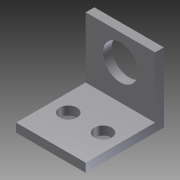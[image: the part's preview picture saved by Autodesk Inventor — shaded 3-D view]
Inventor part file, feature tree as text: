
AUTODESK INVENTOR PART (.ipt)
format: ipt  version: 2012 (Build 160160000, 160)  size: 105,472 bytes
history: native  units: in
note: dims shown in document units (in); Inventor stores cm internally (conversion verified against a paired STEP export)
features: extrude x3, sketch x3
ambient origin geometry x8: Origin, YZ Plane, XZ Plane, XY Plane, X Axis, Y Axis, Z Axis, Center Point
bodies: Solid1 (feature_tree)
feature tree (6):
  extrude  "Extrusion1"  Depth=1.0in
  extrude  "Extrusion2"  Depth=0.125in TaperAngle=0.0deg
  extrude  "Extrusion3"  Depth=1.0in TaperAngle=0.0deg
  sketch  "Sketch1"  dims[d0=1.0in d1=1.0in]
  sketch  "Sketch2"  dims[d2=0.5in d3=0.125in d4=0.0in]
  sketch  "Sketch3"  dims[d5=0.125in d6=1.0in d7=0.0in d8=0.25in d9=0.25in d10=0.25in d11=0.25in d12=0.5in d13=0.5in d14=1.0in d15=0.0in d16=0.375in]
